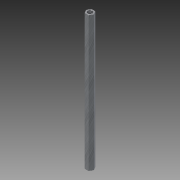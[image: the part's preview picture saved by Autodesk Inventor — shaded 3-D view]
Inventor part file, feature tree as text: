
AUTODESK INVENTOR PART (.ipt)
format: ipt  version: 2011 (Build 150239000, 239)  size: 103,936 bytes
history: native  units: in
note: dims shown in document units (in); Inventor stores cm internally (conversion verified against a paired STEP export)
features: thread x2, other x1, imported_body x1
ambient origin geometry x8: Origin, YZ Plane, XZ Plane, XY Plane, X Axis, Y Axis, Z Axis, Center Point
feature tree (4):
  parser-record x1  (decoder bookkeeping rows leaked as tree rows — omitted from the tree; the rows remain in map.json)
  imported_body  "Base1"
  thread  "Thread1"  [1 undecoded]
  thread  "Thread2"  [1 undecoded]
note: 2 required parameter values undecoded (feature->parameter linkage not recoverable at this tier; creation-order binding heuristic only, values carry confidence <= 0.55)
